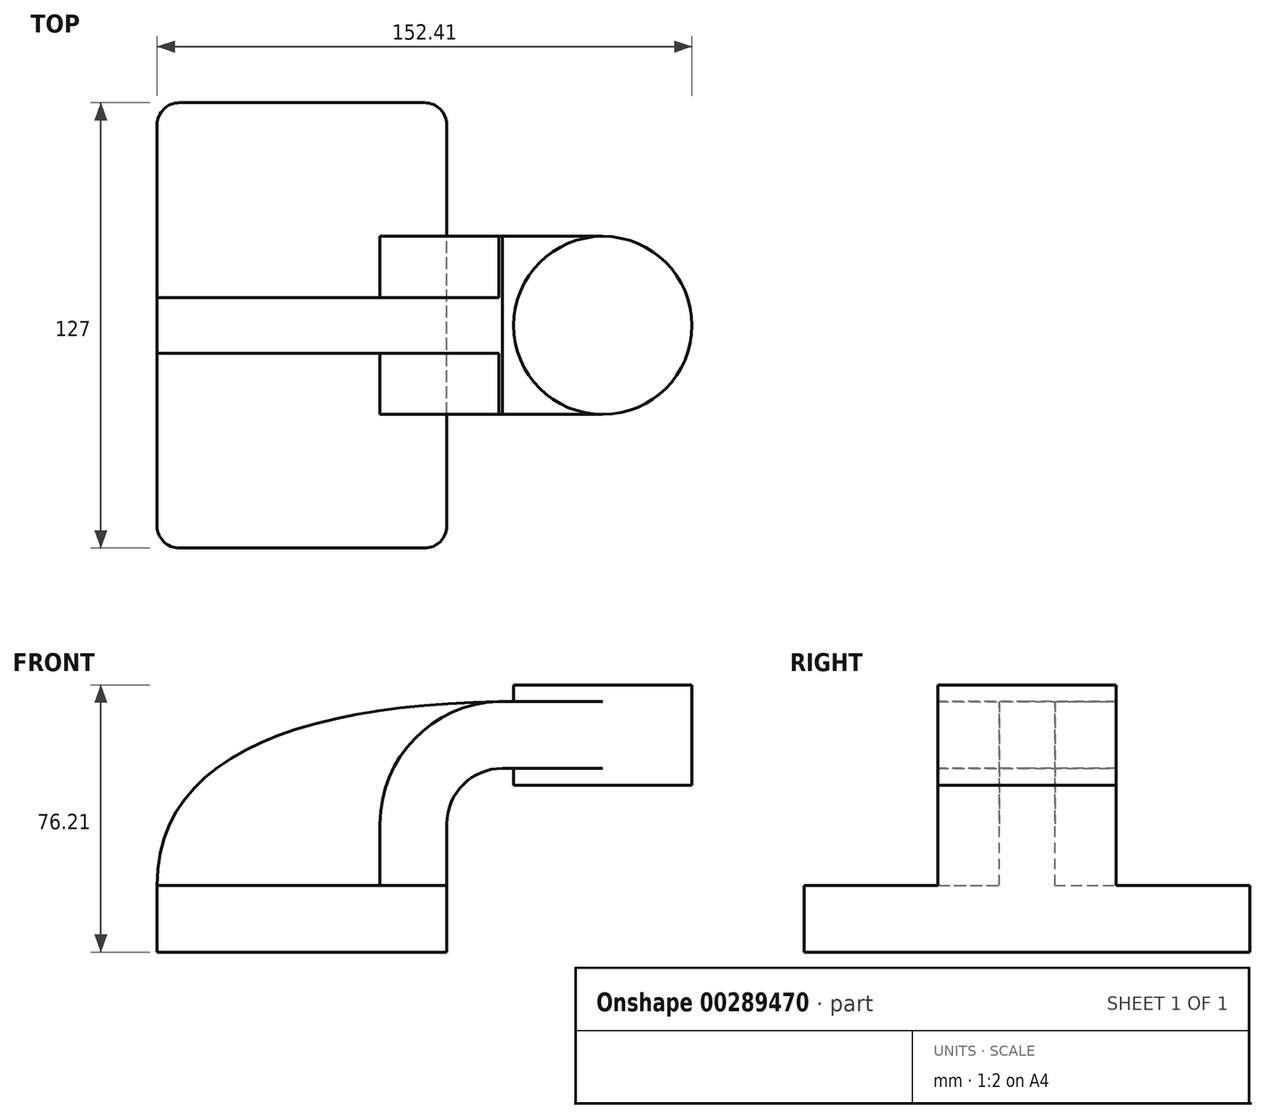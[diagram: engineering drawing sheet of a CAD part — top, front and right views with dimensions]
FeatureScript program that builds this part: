
annotation { "Feature Type Name" : "Feature", "Feature Type Description" : "" }
export const myFeature = defineFeature(function(context is Context, id is Id, definition is map)
    precondition{}
    {
        {
            var Q0;
            Q0=qCreatedBy(makeId("Front.planeOp"),FACE);
            var sketch = newSketch(context, id + "F0", { "sketchPlane" : qUnion([Q0])});
            skLineSegment(sketch, "E0.bottom", {"start": v(41.27, 9.53) * mm, "end": v(-41.28, 9.53) * mm});
            skLineSegment(sketch, "E0.top", {"start": v(41.28, -9.52) * mm, "end": v(-41.27, -9.52) * mm});
            skLineSegment(sketch, "E0.left", {"start": v(41.28, 9.53) * mm, "end": v(41.28, -9.52) * mm});
            skLineSegment(sketch, "E0.right", {"start": v(-41.28, 9.53) * mm, "end": v(-41.28, -9.52) * mm});
            skPoint(sketch, "E0.middle", {"position": v(0, 0) * mm});
            skLineSegment(sketch, "E1.bottom", {"start": v(60.32, 38.1) * mm, "end": v(111.12, 38.1) * mm});
            skLineSegment(sketch, "E1.top", {"start": v(60.33, 66.67) * mm, "end": v(111.12, 66.67) * mm});
            skLineSegment(sketch, "E1.left", {"start": v(60.32, 38.1) * mm, "end": v(60.32, 66.68) * mm});
            skLineSegment(sketch, "E1.right", {"start": v(111.12, 38.1) * mm, "end": v(111.12, 66.67) * mm});
            skPoint(sketch, "E1.middle", {"position": v(85.72, 52.39) * mm});
            skLineSegment(sketch, "E2", {"start": v(41.28, 9.53) * mm, "end": v(41.28, 27) * mm});
            skArc(sketch, "E3", {"start": v(41.28, 27) * mm, "mid": v(45.92, 38.23) * mm, "end": v(57.15, 42.88) * mm});
            skLineSegment(sketch, "E4", {"start": v(57.15, 42.88) * mm, "end": v(85.72, 42.88) * mm});
            skLineSegment(sketch, "E5.0", {"start": v(57.15, 61.93) * mm, "end": v(85.72, 61.93) * mm});
            skArc(sketch, "E5.1", {"start": v(22.23, 27) * mm, "mid": v(32.45, 51.7) * mm, "end": v(57.15, 61.93) * mm});
            skLineSegment(sketch, "E5.2", {"start": v(22.23, 9.53) * mm, "end": v(22.23, 27) * mm});
            skLineSegment(sketch, "E6", {"start": v(85.72, 38.1) * mm, "end": v(85.72, 66.68) * mm});
            skFitSpline(sketch, "E7", {"points": [v(-41.28, 9.53) * mm, v(57.15, 61.93) * mm], "startDerivative": vector(-0.3, 111.74) * mm, "endDerivative": vector(171.45, 2.43) * mm});
            skSolve(sketch);
        }
        {
            var Q0;
            Q0=makeQuery(id+"F0.imprint","IMPRINT",FACE,{"disambiguationData":[TD([[makeQuery(id+"F0.imprint","IMPRINT",EDGE,{"derivedFrom":sQuery(id+"F0.wireOp",EDGE,"E0.top")}),-1.0]])]});
            extrude(context, id + "F1", {"entities" : qUnion([Q0]), "endBound" : BoundingType.SYMMETRIC, "depth" : 127 * mm});
        }
        {
            var Q0;
            {var subQ1=sQuery(id+"F0.wireOp",EDGE,"E2");Q0=makeQuery(id+"F0.imprint","IMPRINT",FACE,{"disambiguationData":[TD([[makeQuery(id+"F0.imprint","IMPRINT",EDGE,{"derivedFrom":subQ1}),1.0]])]});}
            var Q1;
            {var subQ0=sQuery(id+"F0.wireOp",EDGE,"E4");var subQ1=sQuery(id+"F0.wireOp",EDGE,"E1.left");var subQ2=makeQuery(id+"F0.imprint","INTERSECT",VERTEX,{"derivedFrom":[subQ1,subQ0]});Q1=makeQuery(id+"F0.imprint","IMPRINT",FACE,{"disambiguationData":[TD([[makeQuery(id+"F0.imprint","IMPRINT",EDGE,{"disambiguationData":[TD([[subQ2,-1.0]])],"derivedFrom":subQ1}),-1.0]])]});}
            extrude(context, id + "F2", {"entities" : qUnion([Q0, Q1]), "operationType" : NewBodyOperationType.ADD, "endBound" : BoundingType.SYMMETRIC, "depth" : 50.8 * mm});
        }
        {
            var Q0;
            {var subQ3=sQuery(id+"F0.wireOp",EDGE,"E5.2");Q0=makeQuery(id+"F0.imprint","IMPRINT",FACE,{"disambiguationData":[TD([[makeQuery(id+"F0.imprint","IMPRINT",EDGE,{"derivedFrom":subQ3}),1.0]])]});}
            extrude(context, id + "F3", {"entities" : qUnion([Q0]), "operationType" : NewBodyOperationType.ADD, "endBound" : BoundingType.SYMMETRIC, "depth" : 15.88 * mm});
        }
        {
            var Q0;
            {var subQ4=sQuery(id+"F0.wireOp",EDGE,"E1.right");Q0=makeQuery(id+"F0.imprint","IMPRINT",FACE,{"disambiguationData":[TD([[makeQuery(id+"F0.imprint","IMPRINT",EDGE,{"derivedFrom":subQ4}),1.0]])]});}
            var Q1;
            Q1=sQuery(id+"F0.wireOp",EDGE,"E6");
            revolve(context, id + "F4", {"operationType" : NewBodyOperationType.ADD, "entities" : qUnion([Q0]), "axis" : qUnion([Q1]), "revolveType" : RevolveType.FULL});
        }
        {
            var Q0;
            Q0=makeQuery(id+"F1.opExtrude","CAP_EDGE",EDGE,{"disambiguationData":[OSD([sQuery(id+"F0.wireOp",EDGE,"E0.left")])],"isStart":false});
            var Q1;
            Q1=makeQuery(id+"F1.opExtrude","CAP_EDGE",EDGE,{"disambiguationData":[OSD([sQuery(id+"F0.wireOp",EDGE,"E0.left")])],"isStart":true});
            var Q2;
            Q2=makeQuery(id+"F1.opExtrude","CAP_EDGE",EDGE,{"disambiguationData":[OSD([sQuery(id+"F0.wireOp",EDGE,"E0.right")])],"isStart":false});
            var Q3;
            Q3=makeQuery(id+"F1.opExtrude","CAP_EDGE",EDGE,{"disambiguationData":[OSD([sQuery(id+"F0.wireOp",EDGE,"E0.right")])],"isStart":true});
            fillet(context, id + "F5", {"entities" : qUnion([Q0, Q1, Q2, Q3]), "radius" : 6.35 * mm, "tangentPropagation" : true, "allowEdgeOverflow" : false});
        }
    });
